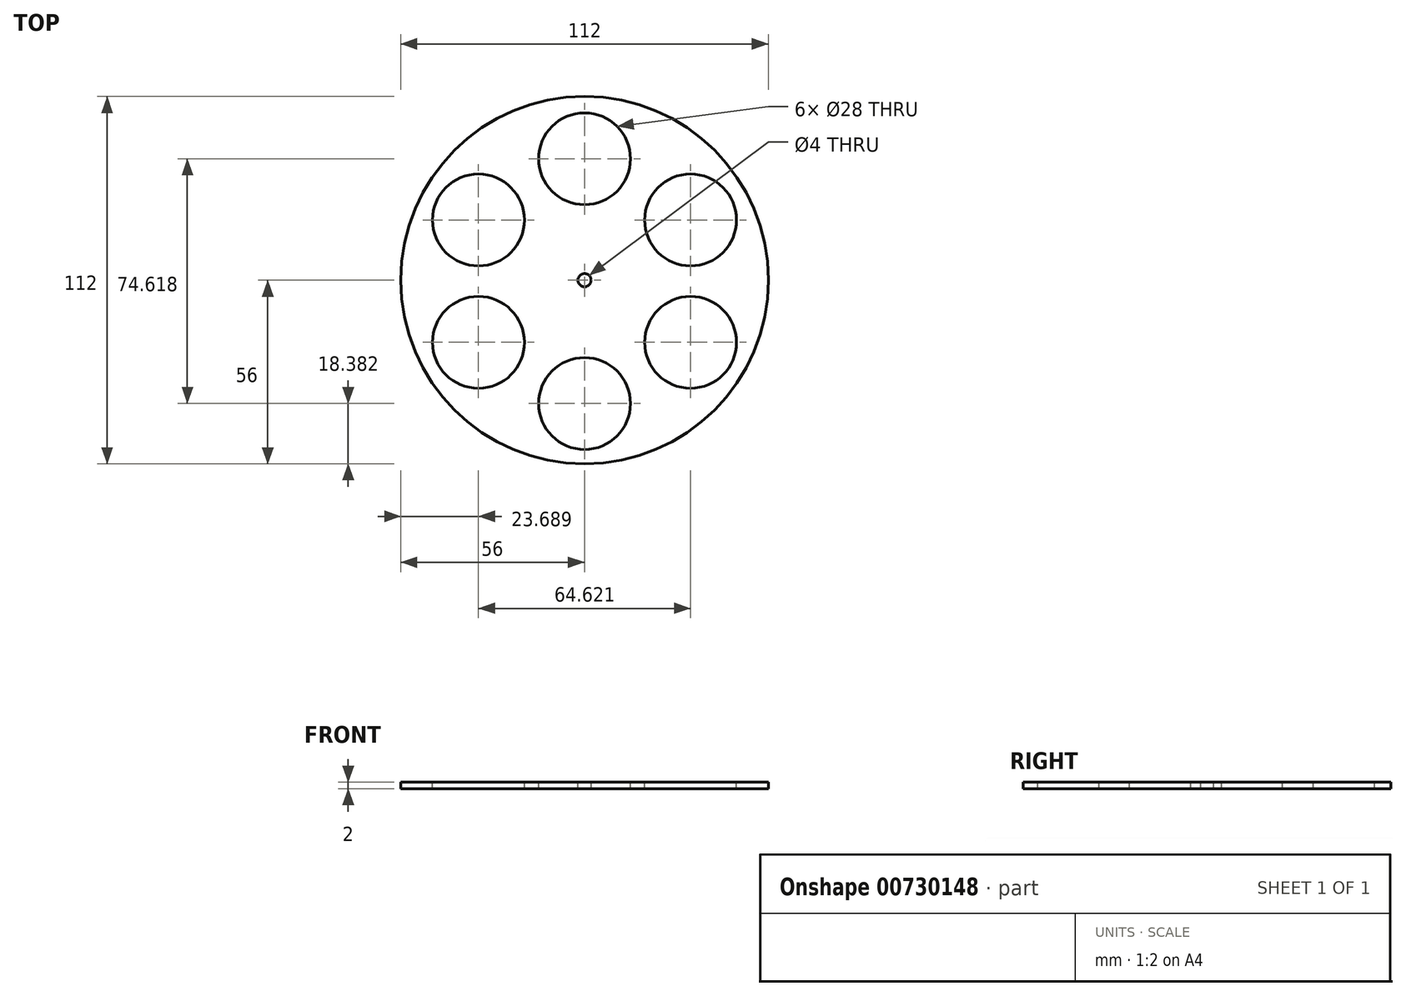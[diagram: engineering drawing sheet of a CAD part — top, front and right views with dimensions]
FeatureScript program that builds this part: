
annotation { "Feature Type Name" : "Feature", "Feature Type Description" : "" }
export const myFeature = defineFeature(function(context is Context, id is Id, definition is map)
    precondition{}
    {
        {
            var Q0;
            Q0=qCreatedBy(makeId("Top.planeOp"),FACE);
            var sketch = newSketch(context, id + "F0", { "sketchPlane" : qUnion([Q0])});
            skCircle(sketch, "E0", {"center": v(0, 0) * mm, "radius": 56 * mm});
            skSolve(sketch);
        }
        {
            var Q0;
            Q0 = qSketchRegion(id + "F0", true);
            extrude(context, id + "F1", {"entities" : qUnion([Q0]), "depth" : 2 * mm, "offsetDistance" : 25 * mm});
        }
        {
            var Q0;
            Q0=makeQuery(id+"F1.opExtrude","CAP_FACE",FACE,{"disambiguationData":[OSD([sQuery(id+"F0.wireOp",EDGE,"E0")])],"isStart":false});
            var sketch = newSketch(context, id + "F2", { "sketchPlane" : qUnion([Q0])});
            skCircle(sketch, "E1", {"center": v(0, 0) * mm, "radius": 2 * mm});
            skSolve(sketch);
        }
        {
            var Q0;
            Q0=makeQuery(id+"F2.imprint","IMPRINT",FACE,{"disambiguationData":[TD([[makeQuery(id+"F2.imprint","IMPRINT",EDGE,{"derivedFrom":sQuery(id+"F2.wireOp",EDGE,"E1")}),1.0]])]});
            extrude(context, id + "F3", {"entities" : qUnion([Q0]), "operationType" : NewBodyOperationType.REMOVE, "oppositeDirection" : true, "depth" : 2 * mm, "offsetDistance" : 25 * mm});
        }
        {
            var Q0;
            Q0=makeQuery(id+"F1.opExtrude","CAP_FACE",FACE,{"disambiguationData":[OSD([sQuery(id+"F0.wireOp",EDGE,"E0")])],"isStart":false});
            var sketch = newSketch(context, id + "F4", { "sketchPlane" : qUnion([Q0])});
            skLineSegment(sketch, "E2", {"start": v(-56, 0) * mm, "end": v(56, 0) * mm, "construction": true});
            skLineSegment(sketch, "E3", {"start": v(0, 56) * mm, "end": v(0, -56) * mm, "construction": true});
            skCircle(sketch, "E4", {"center": v(0, 37) * mm, "radius": 14 * mm});
            skCircle(sketch, "E5.1.0", {"center": v(-32.31, 18.35) * mm, "radius": 14 * mm});
            skCircle(sketch, "E5.2.0", {"center": v(-32.31, -18.96) * mm, "radius": 14 * mm});
            skCircle(sketch, "E5.3.0", {"center": v(0, -37.62) * mm, "radius": 14 * mm});
            skCircle(sketch, "E5.4.0", {"center": v(32.31, -18.96) * mm, "radius": 14 * mm});
            skCircle(sketch, "E5.5.0", {"center": v(32.31, 18.35) * mm, "radius": 14 * mm});
            skPoint(sketch, "E5.center", {"position": v(0, -0.3) * mm});
            skSolve(sketch);
        }
        {
            var Q0;
            Q0 = qSketchRegion(id + "F4", true);
            extrude(context, id + "F5", {"entities" : qUnion([Q0]), "operationType" : NewBodyOperationType.REMOVE, "oppositeDirection" : true, "depth" : 2 * mm, "offsetDistance" : 25 * mm});
        }
    });
